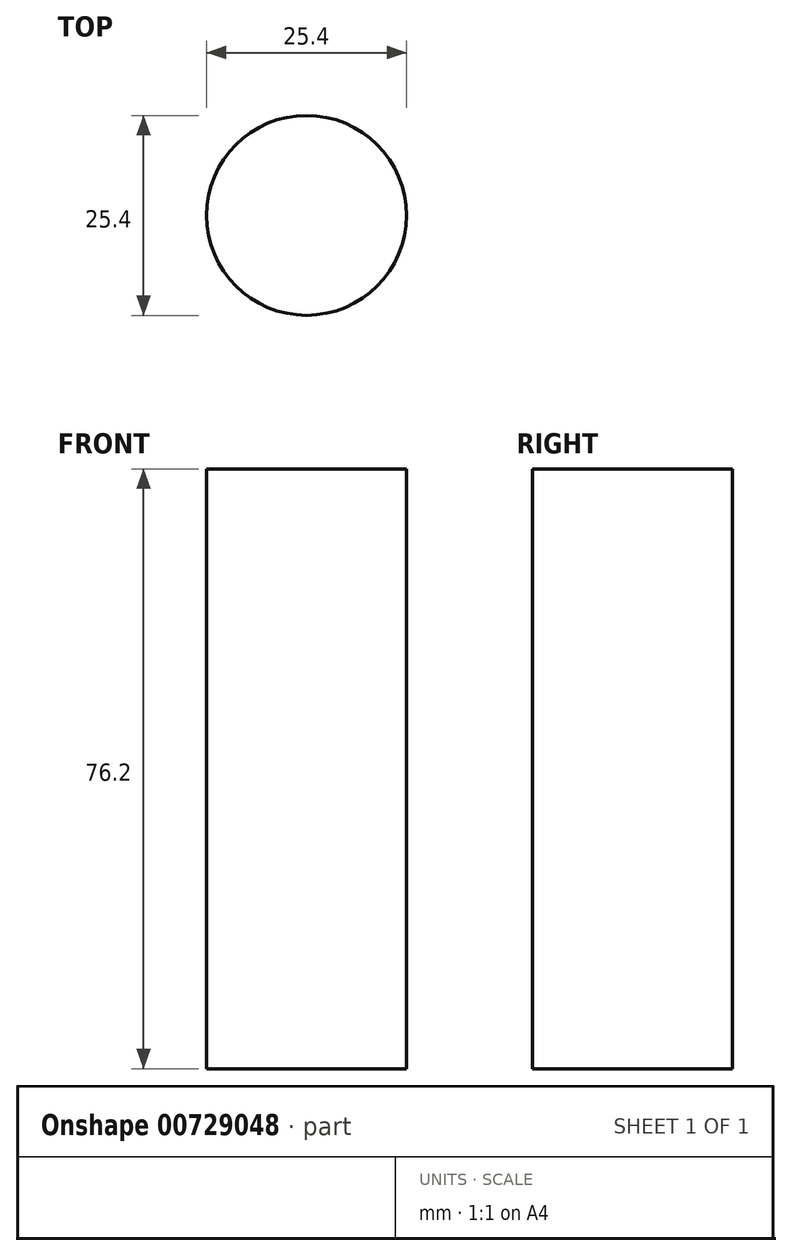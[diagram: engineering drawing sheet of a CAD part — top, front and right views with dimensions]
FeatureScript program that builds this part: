
annotation { "Feature Type Name" : "Feature", "Feature Type Description" : "" }
export const myFeature = defineFeature(function(context is Context, id is Id, definition is map)
    precondition{}
    {
        {
            var Q0;
            Q0=qCreatedBy(makeId("Top.planeOp"),FACE);
            var sketch = newSketch(context, id + "F0", { "sketchPlane" : qUnion([Q0])});
            skCircle(sketch, "E0", {"center": v(0, 0) * mm, "radius": 12.7 * mm});
            skSolve(sketch);
        }
        {
            var Q0;
            Q0 = qSketchRegion(id + "F0", true);
            extrude(context, id + "F1", {"entities" : qUnion([Q0]), "depth" : 76.2 * mm, "offsetDistance" : 25.4 * mm});
        }
    });
